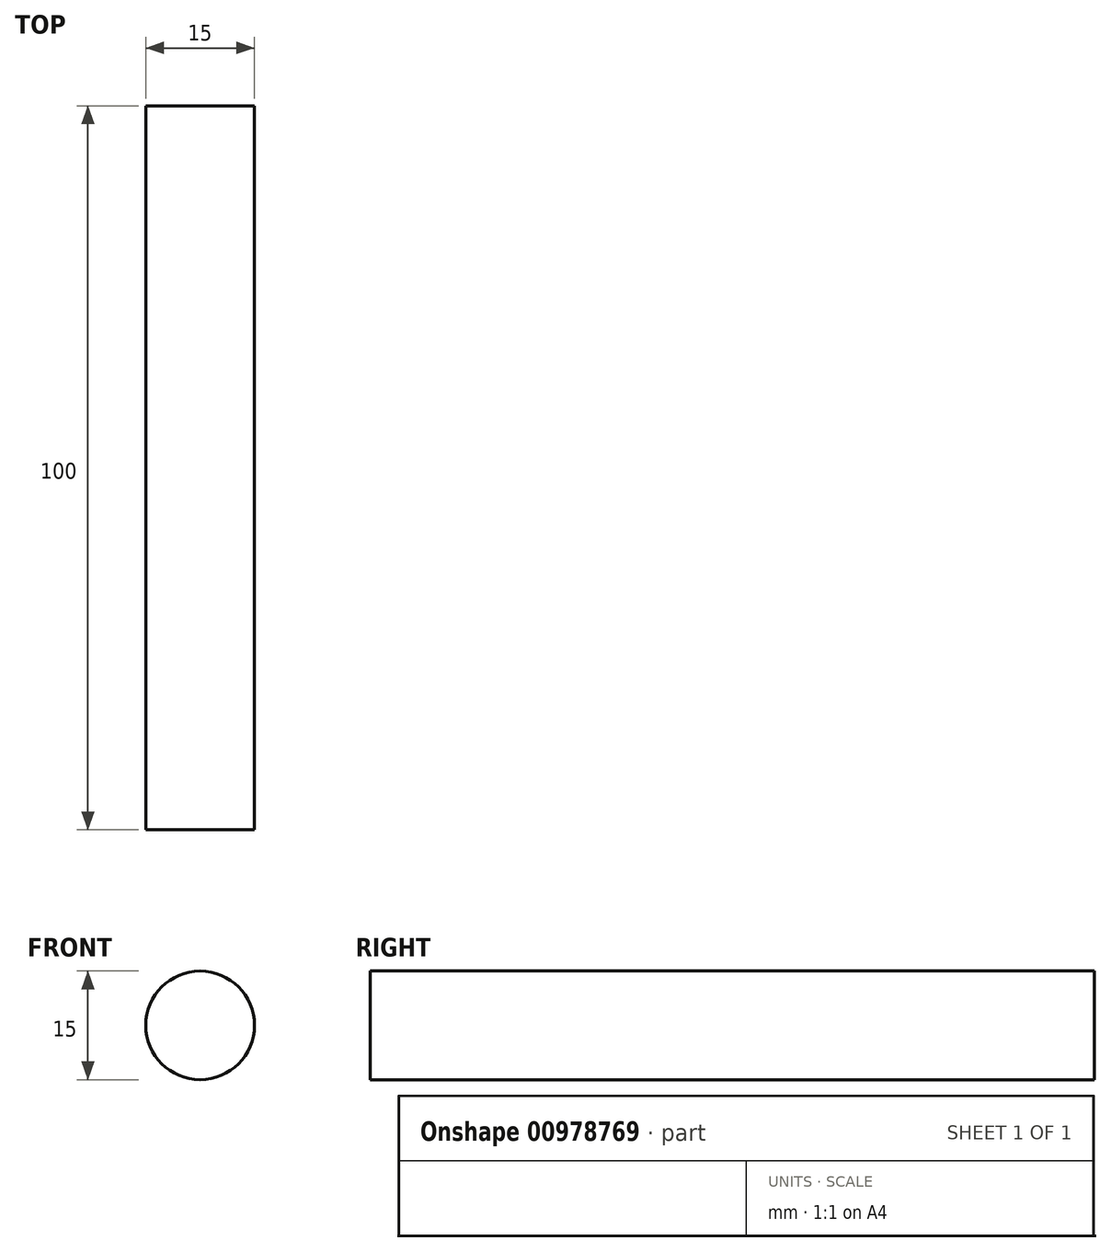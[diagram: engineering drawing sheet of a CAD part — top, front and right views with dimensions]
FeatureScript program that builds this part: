
annotation { "Feature Type Name" : "Feature", "Feature Type Description" : "" }
export const myFeature = defineFeature(function(context is Context, id is Id, definition is map)
    precondition{}
    {
        {
            var Q0;
            Q0=qCreatedBy(makeId("Front.planeOp"),FACE);
            var sketch = newSketch(context, id + "F0", { "sketchPlane" : qUnion([Q0])});
            skCircle(sketch, "E0", {"center": v(0, 0) * mm, "radius": 7.5 * mm});
            skSolve(sketch);
        }
        {
            var Q0;
            Q0 = qSketchRegion(id + "F0", true);
            extrude(context, id + "F1", {"entities" : qUnion([Q0]), "depth" : 100 * mm, "offsetDistance" : 25 * mm});
        }
    });
